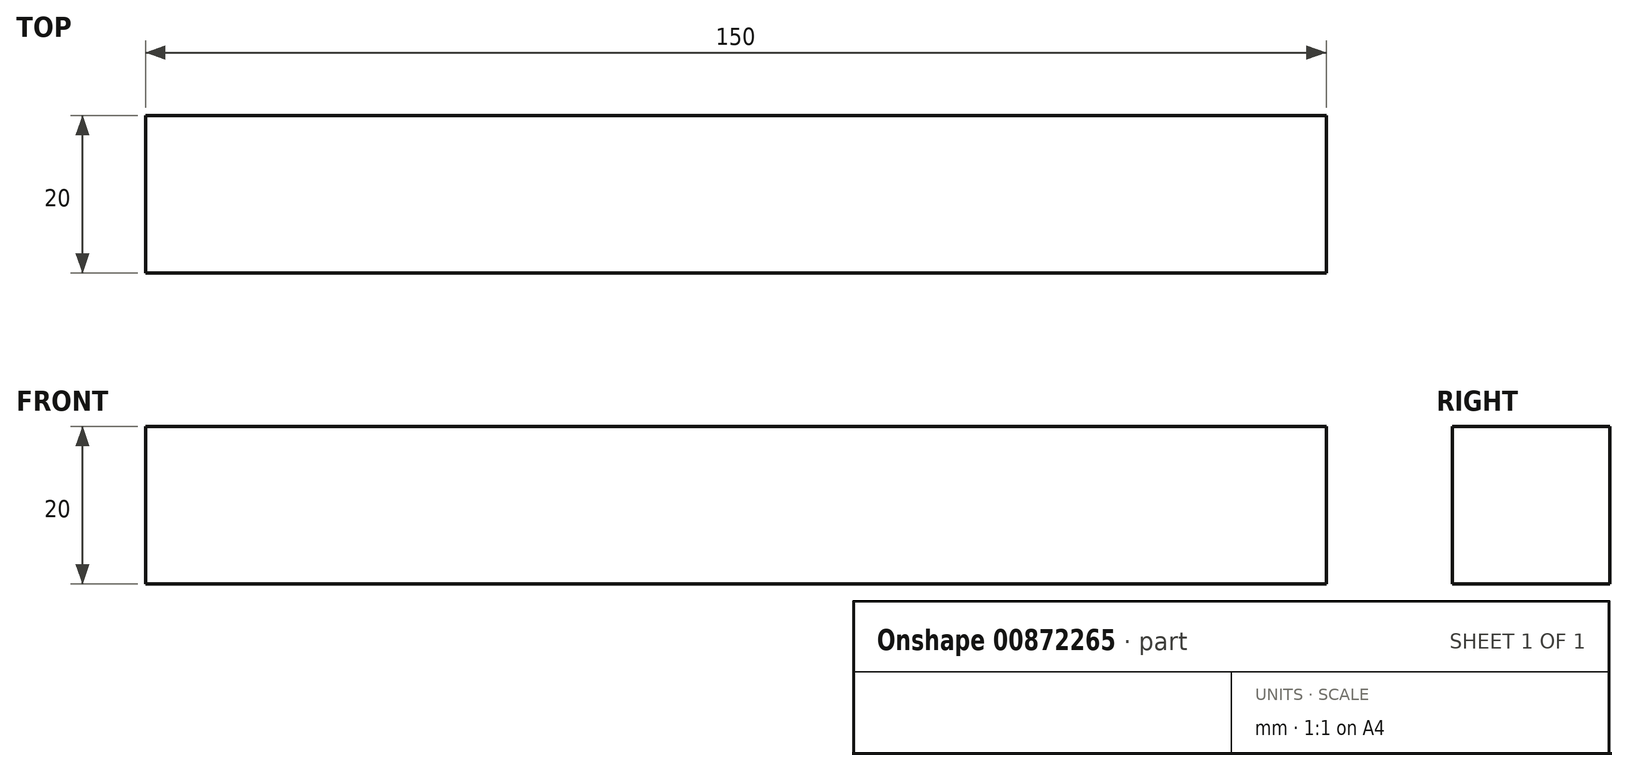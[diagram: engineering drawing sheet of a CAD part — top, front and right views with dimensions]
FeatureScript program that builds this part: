
annotation { "Feature Type Name" : "Feature", "Feature Type Description" : "" }
export const myFeature = defineFeature(function(context is Context, id is Id, definition is map)
    precondition{}
    {
        {
            var Q0;
            Q0=qCreatedBy(makeId("Front.planeOp"),FACE);
            var sketch = newSketch(context, id + "F0", { "sketchPlane" : qUnion([Q0])});
            skLineSegment(sketch, "E0.bottom", {"start": v(75, -10) * mm, "end": v(-75, -10) * mm});
            skLineSegment(sketch, "E0.top", {"start": v(75, 10) * mm, "end": v(-75, 10) * mm});
            skLineSegment(sketch, "E0.left", {"start": v(75, -10) * mm, "end": v(75, 10) * mm});
            skLineSegment(sketch, "E0.right", {"start": v(-75, -10) * mm, "end": v(-75, 10) * mm});
            skPoint(sketch, "E0.middle", {"position": v(0, 0) * mm});
            skSolve(sketch);
        }
        {
            var Q0;
            Q0=makeQuery(id+"F0.imprint","IMPRINT",FACE,{"disambiguationData":[TD([[makeQuery(id+"F0.imprint","IMPRINT",EDGE,{"derivedFrom":sQuery(id+"F0.wireOp",EDGE,"E0.bottom")}),-1.0]])]});
            extrude(context, id + "F1", {"entities" : qUnion([Q0]), "endBound" : BoundingType.SYMMETRIC, "depth" : 20 * mm, "offsetDistance" : 25 * mm});
        }
    });
